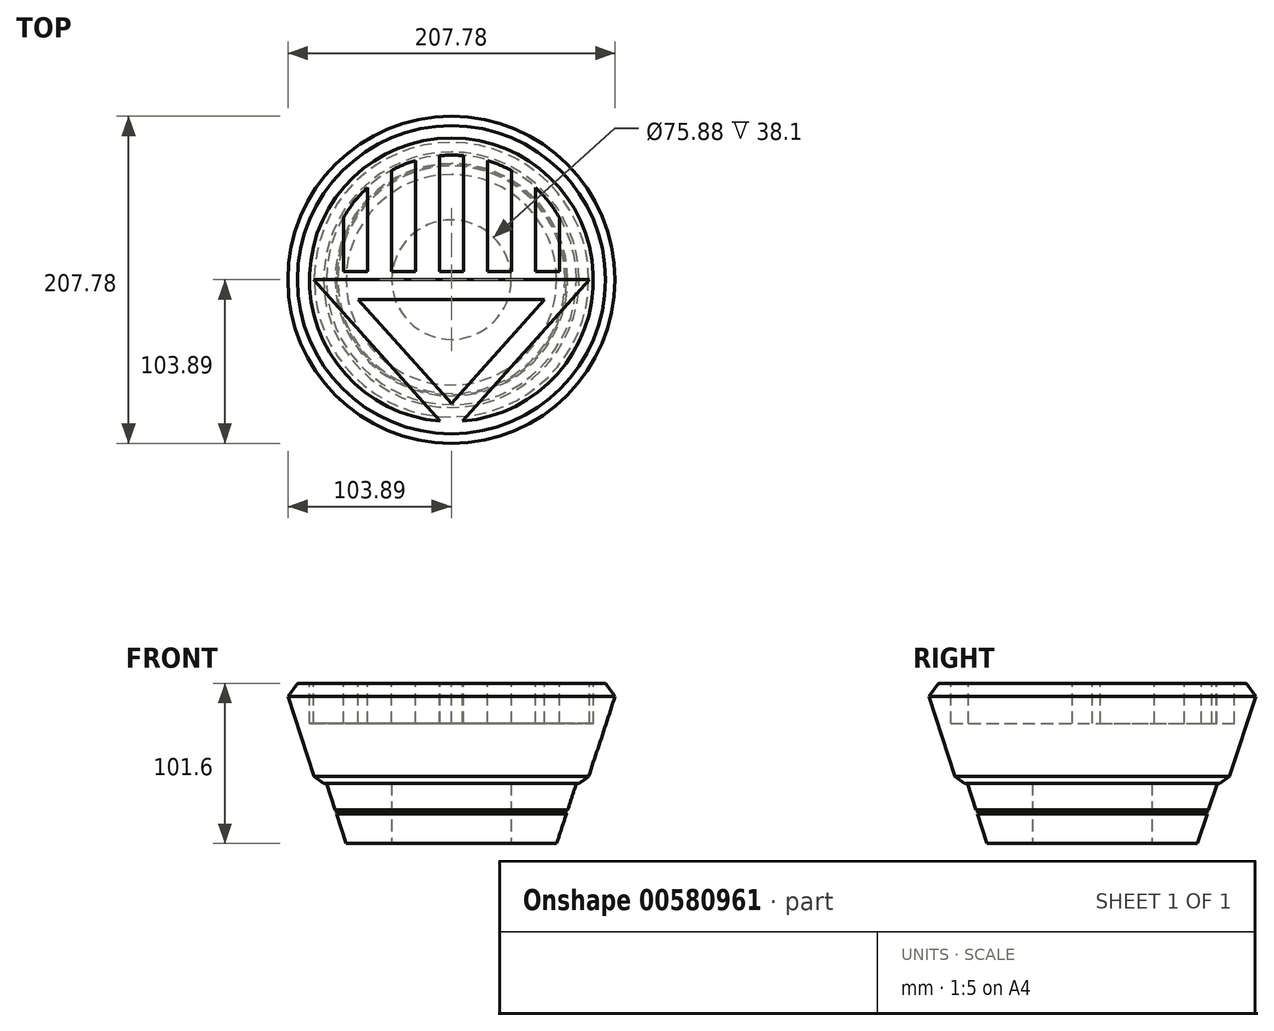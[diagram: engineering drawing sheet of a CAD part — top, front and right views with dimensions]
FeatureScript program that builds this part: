
annotation { "Feature Type Name" : "Feature", "Feature Type Description" : "" }
export const myFeature = defineFeature(function(context is Context, id is Id, definition is map)
    precondition{}
    {
        {
            var Q0;
            Q0=qCreatedBy(makeId("Top.planeOp"),FACE);
            var sketch = newSketch(context, id + "F0", { "sketchPlane" : qUnion([Q0])});
            skCircle(sketch, "E0", {"center": v(0, 0) * mm, "radius": 66.85 * mm});
            skSolve(sketch);
        }
        {
            var Q0;
            Q0=qCreatedBy(makeId("Top.planeOp"),FACE);
            cPlane(context, id + "F1", {"entities" : qUnion([Q0]), "cplaneType" : CPlaneType.OFFSET, "offset" : 101.6 * mm, "width" : 152.4 * mm, "height" : 152.4 * mm});
        }
        {
            var Q0;
            Q0=qCreatedBy(id+"F1.planeOp",FACE);
            var sketch = newSketch(context, id + "F2", { "sketchPlane" : qUnion([Q0])});
            skCircle(sketch, "E1", {"center": v(0, 0) * mm, "radius": 100.28 * mm});
            skSolve(sketch);
        }
        {
            var Q0;
            Q0=makeQuery(id+"F2.imprint","IMPRINT",FACE,{"disambiguationData":[TD([[makeQuery(id+"F2.imprint","IMPRINT",EDGE,{"derivedFrom":sQuery(id+"F2.wireOp",EDGE,"E1")}),1.0]])]});
            var Q1;
            Q1=makeQuery(id+"F0.imprint","IMPRINT",FACE,{"disambiguationData":[TD([[makeQuery(id+"F0.imprint","IMPRINT",EDGE,{"derivedFrom":sQuery(id+"F0.wireOp",EDGE,"E0")}),1.0]])]});
            var Q2;
            Q2=sQuery(id+"F2.wireOp",EDGE,"Eyu8YDiN-lEGU-Wuxt-0ncA-RZLAWeJK4OgB");
            var Q3;
            Q3=sQuery(id+"F0.wireOp",EDGE,"fgfE4CqQ-t5n6-ucAx-yhIW-5wF2yx0Jya2k");
            loft(context, id + "F3", {"sheetProfilesArray" : [{ "sheetProfileEntities" : qUnion([Q0]) }, { "sheetProfileEntities" : qUnion([Q1]) }], "wireProfilesArray" : [{ "wireProfileEntities" : qUnion([Q2]) }, { "wireProfileEntities" : qUnion([Q3]) }]});
        }
        {
            var Q0;
            Q0=qCreatedBy(makeId("Top.planeOp"),FACE);
            var sketch = newSketch(context, id + "F4", { "sketchPlane" : qUnion([Q0])});
            skCircle(sketch, "E2", {"center": v(0, 0) * mm, "radius": 37.94 * mm});
            skSolve(sketch);
        }
        {
            var Q0;
            Q0=makeQuery(id+"F4.imprint","IMPRINT",FACE,{"disambiguationData":[TD([[makeQuery(id+"F4.imprint","IMPRINT",EDGE,{"derivedFrom":sQuery(id+"F4.wireOp",EDGE,"E2")}),1.0]])]});
            extrude(context, id + "F5", {"entities" : qUnion([Q0]), "operationType" : NewBodyOperationType.REMOVE, "depth" : 53.34 * mm, "offsetDistance" : 25.4 * mm});
        }
        {
            var Q0;
            Q0=qCreatedBy(makeId("Top.planeOp"),FACE);
            cPlane(context, id + "F6", {"entities" : qUnion([Q0]), "cplaneType" : CPlaneType.OFFSET, "offset" : 38.1 * mm, "width" : 152.4 * mm, "height" : 152.4 * mm});
        }
        {
            var Q0;
            Q0=qCreatedBy(id+"F6.planeOp",FACE);
            var sketch = newSketch(context, id + "F7", { "sketchPlane" : qUnion([Q0])});
            skCircle(sketch, "E3", {"center": v(0, 0) * mm, "radius": 85.73 * mm});
            skSolve(sketch);
        }
        {
            var Q0;
            Q0=qCreatedBy(id+"F1.planeOp",FACE);
            var sketch = newSketch(context, id + "F8", { "sketchPlane" : qUnion([Q0])});
            skCircle(sketch, "E4", {"center": v(0, 0) * mm, "radius": 106.63 * mm});
            skSolve(sketch);
        }
        {
            var Q1;
            Q1=makeQuery(id+"F7.imprint","IMPRINT",FACE,{"disambiguationData":[TD([[makeQuery(id+"F7.imprint","IMPRINT",EDGE,{"derivedFrom":sQuery(id+"F7.wireOp",EDGE,"E3")}),1.0]])]});
            var Q2;
            Q2=makeQuery(id+"F8.imprint","IMPRINT",FACE,{"disambiguationData":[TD([[makeQuery(id+"F8.imprint","IMPRINT",EDGE,{"derivedFrom":sQuery(id+"F8.wireOp",EDGE,"E4")}),1.0]])]});
            loft(context, id + "F9", {"operationType" : NewBodyOperationType.ADD, "sheetProfilesArray" : [{ "sheetProfileEntities" : qUnion([Q1]) }, { "sheetProfileEntities" : qUnion([Q2]) }]});
        }
        {
            var Q0;
            Q0=makeQuery(id+"F9.opLoft","MID_CAP_EDGE",EDGE,{"disambiguationData":[OSD([sQuery(id+"F7.wireOp",EDGE,"E3")])],"capPos":0.0});
            chamfer(context, id + "F10", {"entities" : qUnion([Q0]), "width" : 6.35 * mm, "tangentPropagation" : true});
        }
        {
            var Q0;
            Q0=makeQuery(id+"F9.opLoft","MID_CAP_EDGE",EDGE,{"disambiguationData":[OSD([sQuery(id+"F7.wireOp",EDGE,"E3"),sQuery(id+"F8.wireOp",EDGE,"E4")])],"capPos":1.0});
            chamfer(context, id + "F11", {"entities" : qUnion([Q0]), "width" : 6.35 * mm, "tangentPropagation" : true});
        }
        {
            var Q0;
            Q0=qCreatedBy(makeId("Front.planeOp"),FACE);
            var sketch = newSketch(context, id + "F12", { "sketchPlane" : qUnion([Q0])});
            skLineSegment(sketch, "E5", {"start": v(-79.4, 38.11) * mm, "end": v(-66.85, 0) * mm});
            skLineSegment(sketch, "E6", {"start": v(-73.8, 21.14) * mm, "end": v(-72.2, 20.33) * mm});
            skLineSegment(sketch, "E7", {"start": v(-72.2, 20.33) * mm, "end": v(-73.02, 18.73) * mm});
            skSolve(sketch);
        }
        {
            var Q0;
            Q0=qCreatedBy(makeId("Right.planeOp"),FACE);
            var sketch = newSketch(context, id + "F13", { "sketchPlane" : qUnion([Q0])});
            skLineSegment(sketch, "E8", {"start": v(0, 0) * mm, "end": v(0, 184.2) * mm});
            skSolve(sketch);
        }
        {
            var Q0;
            Q0=qSketchRegion(id+"F12",true);
            var Q1;
            Q1=sQuery(id+"F13.wireOp",EDGE,"E8");
            revolve(context, id + "F14", {"operationType" : NewBodyOperationType.REMOVE, "entities" : qUnion([Q0]), "axis" : qUnion([Q1]), "revolveType" : RevolveType.FULL, "oppositeDirection" : true});
        }
        {
            var Q0;
            Q0=makeQuery(id+"F9.boolean.opBoolean","MERGE",FACE,{"derivedFrom":[makeQuery(id+"F3.opLoft","CAP_FACE",FACE,{"disambiguationData":[OSD([makeQuery(id+"F2.imprint","IMPRINT",FACE,{"disambiguationData":[TD([[makeQuery(id+"F2.imprint","IMPRINT",EDGE,{"derivedFrom":sQuery(id+"F2.wireOp",EDGE,"E1")}),1.0]])]})])],"isStart":true}),makeQuery(id+"F9.opLoft","CAP_FACE",FACE,{"disambiguationData":[OSD([makeQuery(id+"F8.imprint","IMPRINT",FACE,{"disambiguationData":[TD([[makeQuery(id+"F8.imprint","IMPRINT",EDGE,{"derivedFrom":sQuery(id+"F8.wireOp",EDGE,"E4")}),1.0]])]})])],"isStart":true})]});
            var sketch = newSketch(context, id + "F15", { "sketchPlane" : qUnion([Q0])});
            skCircle(sketch, "E9", {"center": v(0, 0) * mm, "radius": 100.28 * mm});
            skCircle(sketch, "E10.0", {"center": v(0, 0) * mm, "radius": 90.12 * mm});
            skLineSegment(sketch, "E11", {"start": v(-87.58, 0) * mm, "end": v(87.58, 0) * mm});
            skLineSegment(sketch, "E12", {"start": v(87.58, 0) * mm, "end": v(0, -97.74) * mm});
            skLineSegment(sketch, "E13", {"start": v(0, -97.74) * mm, "end": v(-87.58, 0) * mm});
            skLineSegment(sketch, "E14.0", {"start": v(-59.15, -12.7) * mm, "end": v(59.15, -12.7) * mm});
            skLineSegment(sketch, "E14.1", {"start": v(0, -78.7) * mm, "end": v(-59.15, -12.7) * mm});
            skLineSegment(sketch, "E14.2", {"start": v(59.15, -12.7) * mm, "end": v(0, -78.7) * mm});
            skLineSegment(sketch, "E15.bottom", {"start": v(7.62, 5.08) * mm, "end": v(-7.62, 5.08) * mm});
            skLineSegment(sketch, "E15.top", {"start": v(7.62, 89.8) * mm, "end": v(-7.62, 89.8) * mm});
            skLineSegment(sketch, "E15.left", {"start": v(7.62, 5.08) * mm, "end": v(7.62, 89.8) * mm});
            skLineSegment(sketch, "E15.right", {"start": v(-7.62, 5.08) * mm, "end": v(-7.62, 89.8) * mm});
            skLineSegment(sketch, "E16.bottom", {"start": v(-22.86, 5.08) * mm, "end": v(-38.1, 5.08) * mm});
            skLineSegment(sketch, "E16.top", {"start": v(-22.86, 81.67) * mm, "end": v(-38.1, 81.67) * mm});
            skLineSegment(sketch, "E16.left", {"start": v(-22.86, 5.08) * mm, "end": v(-22.86, 81.67) * mm});
            skLineSegment(sketch, "E16.right", {"start": v(-38.1, 5.08) * mm, "end": v(-38.1, 81.67) * mm});
            skLineSegment(sketch, "E17.bottom", {"start": v(-53.34, 5.08) * mm, "end": v(-68.58, 5.08) * mm});
            skLineSegment(sketch, "E17.top", {"start": v(-53.34, 58.47) * mm, "end": v(-68.58, 58.47) * mm});
            skLineSegment(sketch, "E17.left", {"start": v(-53.34, 5.08) * mm, "end": v(-53.34, 58.47) * mm});
            skLineSegment(sketch, "E17.right", {"start": v(-68.58, 5.08) * mm, "end": v(-68.58, 58.47) * mm});
            skLineSegment(sketch, "E18", {"start": v(0, 0) * mm, "end": v(0, 11.87) * mm});
            skLineSegment(sketch, "E19.MirrorCS", {"start": v(68.58, 5.08) * mm, "end": v(68.58, 58.47) * mm});
            skLineSegment(sketch, "E20.MirrorCS", {"start": v(53.34, 58.47) * mm, "end": v(68.58, 58.47) * mm});
            skLineSegment(sketch, "E21.MirrorCS", {"start": v(53.34, 5.08) * mm, "end": v(68.58, 5.08) * mm});
            skLineSegment(sketch, "E22.MirrorCS", {"start": v(53.34, 5.08) * mm, "end": v(53.34, 58.47) * mm});
            skLineSegment(sketch, "E23.MirrorCS", {"start": v(38.1, 5.08) * mm, "end": v(38.1, 81.67) * mm});
            skLineSegment(sketch, "E24.MirrorCS", {"start": v(22.86, 5.08) * mm, "end": v(22.86, 81.67) * mm});
            skLineSegment(sketch, "E25.MirrorCS", {"start": v(22.86, 81.67) * mm, "end": v(38.1, 81.67) * mm});
            skLineSegment(sketch, "E26.MirrorCS", {"start": v(22.86, 5.08) * mm, "end": v(38.1, 5.08) * mm});
            skCircle(sketch, "E27", {"center": v(0, 0) * mm, "radius": 79.14 * mm});
            skSolve(sketch);
        }
        {
            var Q0;
            {var subQ0=sQuery(id+"F15.wireOp",EDGE,"2d981b6a-a36c-429e-8e7e-1961ac6362790.MirrorCS");var subQ1=sQuery(id+"F15.wireOp",EDGE,"K4UFzg29-vVcX-KDtk-gjHo-bnuy8YvNwfuU");var subQ2=makeQuery(id+"F15.imprint","INTERSECT",VERTEX,{"derivedFrom":[subQ1,subQ0]});Q0=makeQuery(id+"F15.imprint","IMPRINT",FACE,{"disambiguationData":[TD([[makeQuery(id+"F15.imprint","IMPRINT",EDGE,{"disambiguationData":[TD([[subQ2,-1.0]])],"derivedFrom":subQ1}),-1.0]])]});}
            var Q1;
            Q1=makeQuery(id+"F15.imprint","IMPRINT",FACE,{"disambiguationData":[TD([[makeQuery(id+"F15.imprint","IMPRINT",EDGE,{"derivedFrom":sQuery(id+"F15.wireOp",EDGE,"E10.0")}),1.0]])]});
            var Q2;
            Q2=makeQuery(id+"F15.imprint","IMPRINT",FACE,{"disambiguationData":[TD([[makeQuery(id+"F15.imprint","IMPRINT",EDGE,{"derivedFrom":sQuery(id+"F15.wireOp",EDGE,"3ecf9a04-cdc3-40a6-907b-ea063ad2b2e0.0")}),1.0]])]});
            var Q3;
            {var subQ0=sQuery(id+"F15.wireOp",EDGE,"f71a98ee-37c5-4e0d-85ec-4346386b53170.MirrorCS");var subQ1=sQuery(id+"F15.wireOp",EDGE,"K4UFzg29-vVcX-KDtk-gjHo-bnuy8YvNwfuU");var subQ2=makeQuery(id+"F15.imprint","INTERSECT",VERTEX,{"derivedFrom":[subQ1,subQ0]});Q3=makeQuery(id+"F15.imprint","IMPRINT",FACE,{"disambiguationData":[TD([[makeQuery(id+"F15.imprint","IMPRINT",EDGE,{"disambiguationData":[TD([[subQ2,-1.0]])],"derivedFrom":subQ1}),-1.0]])]});}
            var Q4;
            Q4=makeQuery(id+"F15.imprint","IMPRINT",FACE,{"disambiguationData":[TD([[makeQuery(id+"F15.imprint","IMPRINT",EDGE,{"derivedFrom":sQuery(id+"F15.wireOp",EDGE,"UvbLV0dz-3cuz-Rr9D-HXqz-MAaWx83NbRCh")}),1.0]])]});
            var Q5;
            {var subQ0=sQuery(id+"F15.wireOp",EDGE,"E14.0");Q5=makeQuery(id+"F15.imprint","IMPRINT",FACE,{"disambiguationData":[TD([[makeQuery(id+"F15.imprint","IMPRINT",EDGE,{"derivedFrom":subQ0}),-1.0]])]});}
            var Q6;
            {var subQ0=sQuery(id+"F15.wireOp",EDGE,"E27");var subQ1=sQuery(id+"F15.wireOp",EDGE,"E13");var subQ2=makeQuery(id+"F15.imprint","INTERSECT",VERTEX,{"disambiguationData":[OD(0.0)],"derivedFrom":[subQ1,subQ0]});Q6=makeQuery(id+"F15.imprint","IMPRINT",FACE,{"disambiguationData":[TD([[makeQuery(id+"F15.imprint","IMPRINT",EDGE,{"disambiguationData":[TD([[subQ2,-1.0]])],"derivedFrom":subQ1}),1.0]])]});}
            var Q7;
            {var subQ0=sQuery(id+"F15.wireOp",EDGE,"E13");var subQ1=sQuery(id+"F15.wireOp",EDGE,"E11");var subQ2=makeQuery(id+"F15.imprint","INTERSECT",VERTEX,{"derivedFrom":[subQ1,subQ0]});Q7=makeQuery(id+"F15.imprint","IMPRINT",FACE,{"disambiguationData":[TD([[makeQuery(id+"F15.imprint","IMPRINT",EDGE,{"disambiguationData":[TD([[subQ2,-1.0]])],"derivedFrom":subQ1}),1.0]])]});}
            var Q8;
            {var subQ0=sQuery(id+"F15.wireOp",EDGE,"E27");var subQ1=sQuery(id+"F15.wireOp",EDGE,"E12");var subQ2=makeQuery(id+"F15.imprint","INTERSECT",VERTEX,{"disambiguationData":[OD(0.0)],"derivedFrom":[subQ1,subQ0]});Q8=makeQuery(id+"F15.imprint","IMPRINT",FACE,{"disambiguationData":[TD([[makeQuery(id+"F15.imprint","IMPRINT",EDGE,{"disambiguationData":[TD([[subQ2,-1.0]])],"derivedFrom":subQ1}),1.0]])]});}
            var Q9;
            {var subQ0=sQuery(id+"F15.wireOp",EDGE,"E12");var subQ5=sQuery(id+"F15.wireOp",EDGE,"E11");var subQ6=makeQuery(id+"F15.imprint","INTERSECT",VERTEX,{"derivedFrom":[subQ5,subQ0]});Q9=makeQuery(id+"F15.imprint","IMPRINT",FACE,{"disambiguationData":[TD([[makeQuery(id+"F15.imprint","IMPRINT",EDGE,{"disambiguationData":[TD([[subQ6,1.0]])],"derivedFrom":subQ5}),1.0]])]});}
            var Q10;
            {var subQ0=sQuery(id+"F15.wireOp",EDGE,"E14.2");var subQ1=sQuery(id+"F15.wireOp",EDGE,"E14.1");var subQ2=makeQuery(id+"F15.imprint","INTERSECT",VERTEX,{"derivedFrom":[subQ1,subQ0]});Q10=makeQuery(id+"F15.imprint","IMPRINT",FACE,{"disambiguationData":[TD([[makeQuery(id+"F15.imprint","IMPRINT",EDGE,{"disambiguationData":[TD([[subQ2,-1.0]])],"derivedFrom":subQ1}),-1.0]])]});}
            var Q11;
            {var subQ0=sQuery(id+"F15.wireOp",EDGE,"E17.top");Q11=makeQuery(id+"F15.imprint","IMPRINT",FACE,{"disambiguationData":[TD([[makeQuery(id+"F15.imprint","IMPRINT",EDGE,{"derivedFrom":subQ0}),1.0]])]});}
            var Q12;
            {var subQ3=sQuery(id+"F15.wireOp",EDGE,"E17.top");Q12=makeQuery(id+"F15.imprint","IMPRINT",FACE,{"disambiguationData":[TD([[makeQuery(id+"F15.imprint","IMPRINT",EDGE,{"derivedFrom":subQ3}),-1.0]])]});}
            var Q13;
            {var subQ0=sQuery(id+"F15.wireOp",EDGE,"E16.top");Q13=makeQuery(id+"F15.imprint","IMPRINT",FACE,{"disambiguationData":[TD([[makeQuery(id+"F15.imprint","IMPRINT",EDGE,{"derivedFrom":subQ0}),1.0]])]});}
            var Q14;
            {var subQ1=sQuery(id+"F15.wireOp",EDGE,"E16.top");Q14=makeQuery(id+"F15.imprint","IMPRINT",FACE,{"disambiguationData":[TD([[makeQuery(id+"F15.imprint","IMPRINT",EDGE,{"derivedFrom":subQ1}),-1.0]])]});}
            var Q15;
            {var subQ0=sQuery(id+"F15.wireOp",EDGE,"E15.top");Q15=makeQuery(id+"F15.imprint","IMPRINT",FACE,{"disambiguationData":[TD([[makeQuery(id+"F15.imprint","IMPRINT",EDGE,{"derivedFrom":subQ0}),1.0]])]});}
            var Q16;
            {var subQ0=sQuery(id+"F15.wireOp",EDGE,"E25.MirrorCS");Q16=makeQuery(id+"F15.imprint","IMPRINT",FACE,{"disambiguationData":[TD([[makeQuery(id+"F15.imprint","IMPRINT",EDGE,{"derivedFrom":subQ0}),1.0]])]});}
            var Q17;
            {var subQ0=sQuery(id+"F15.wireOp",EDGE,"E25.MirrorCS");Q17=makeQuery(id+"F15.imprint","IMPRINT",FACE,{"disambiguationData":[TD([[makeQuery(id+"F15.imprint","IMPRINT",EDGE,{"derivedFrom":subQ0}),-1.0]])]});}
            var Q18;
            {var subQ0=sQuery(id+"F15.wireOp",EDGE,"E20.MirrorCS");Q18=makeQuery(id+"F15.imprint","IMPRINT",FACE,{"disambiguationData":[TD([[makeQuery(id+"F15.imprint","IMPRINT",EDGE,{"derivedFrom":subQ0}),1.0]])]});}
            var Q19;
            {var subQ0=sQuery(id+"F15.wireOp",EDGE,"E20.MirrorCS");Q19=makeQuery(id+"F15.imprint","IMPRINT",FACE,{"disambiguationData":[TD([[makeQuery(id+"F15.imprint","IMPRINT",EDGE,{"derivedFrom":subQ0}),-1.0]])]});}
            var Q20;
            {var subQ13=sQuery(id+"F15.wireOp",EDGE,"E21.MirrorCS");Q20=makeQuery(id+"F15.imprint","IMPRINT",FACE,{"disambiguationData":[TD([[makeQuery(id+"F15.imprint","IMPRINT",EDGE,{"derivedFrom":subQ13}),-1.0]])]});}
            var Q21;
            {var subQ9=sQuery(id+"F15.wireOp",EDGE,"E16.bottom");Q21=makeQuery(id+"F15.imprint","IMPRINT",FACE,{"disambiguationData":[TD([[makeQuery(id+"F15.imprint","IMPRINT",EDGE,{"derivedFrom":subQ9}),1.0]])]});}
            extrude(context, id + "F16", {"entities" : qUnion([Q0, Q1, Q2, Q3, Q4, Q5, Q6, Q7, Q8, Q9, Q10, Q11, Q12, Q13, Q14, Q15, Q16, Q17, Q18, Q19, Q20, Q21]), "operationType" : NewBodyOperationType.REMOVE, "oppositeDirection" : true, "depth" : 25.4 * mm, "offsetDistance" : 25.4 * mm});
        }
    });
